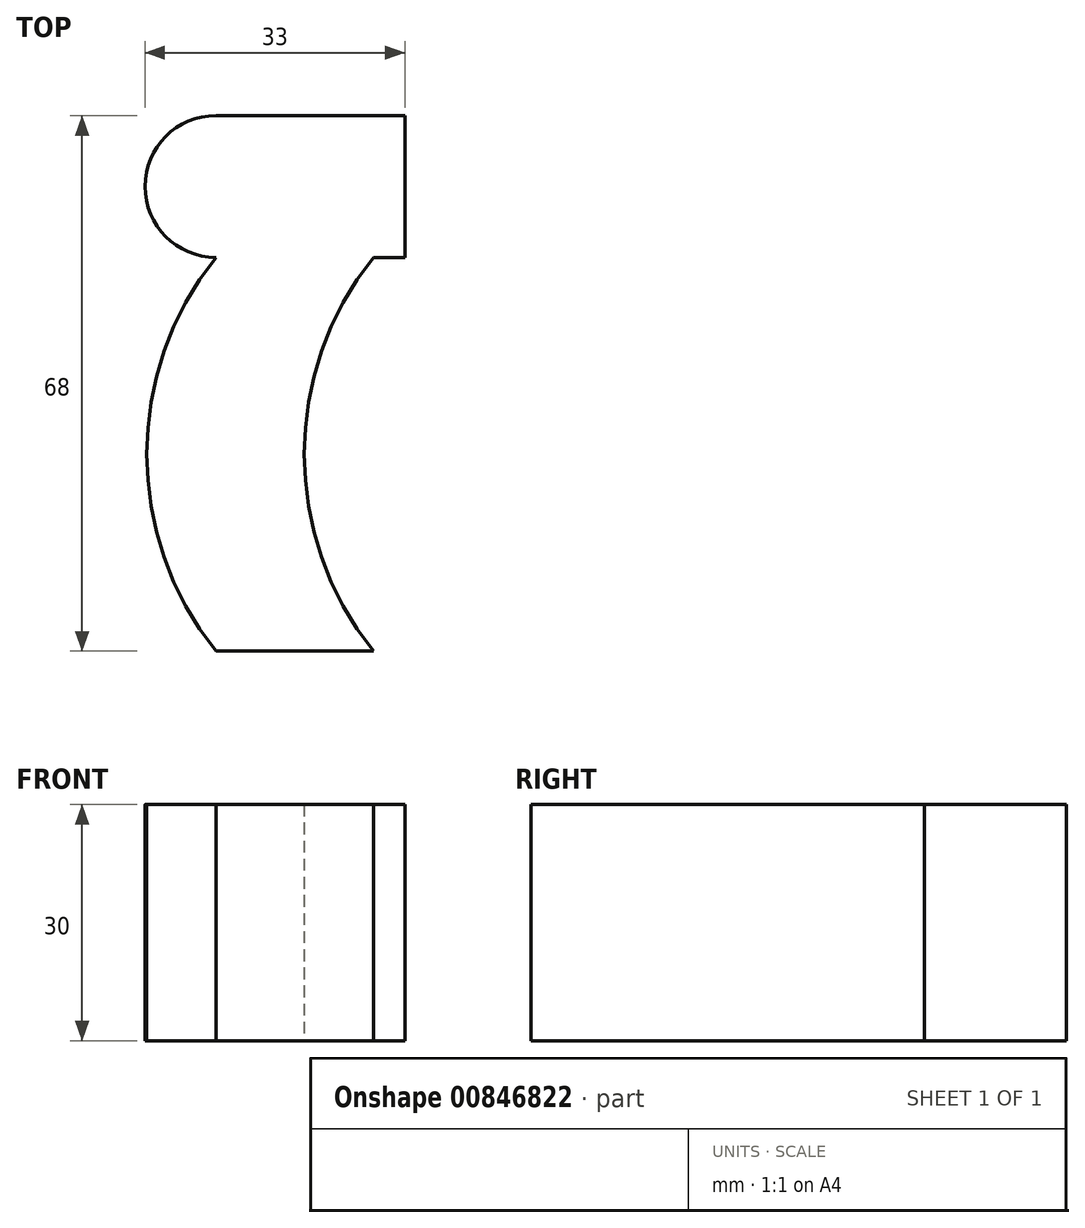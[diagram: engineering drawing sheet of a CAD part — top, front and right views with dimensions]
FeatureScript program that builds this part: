
annotation { "Feature Type Name" : "Feature", "Feature Type Description" : "" }
export const myFeature = defineFeature(function(context is Context, id is Id, definition is map)
    precondition{}
    {
        {
            var Q0;
            Q0=qCreatedBy(makeId("Top.planeOp"),FACE);
            var sketch = newSketch(context, id + "F0", { "sketchPlane" : qUnion([Q0])});
            skLineSegment(sketch, "E0", {"start": v(-2.92, -33.1) * mm, "end": v(17.08, -33.1) * mm});
            skArc(sketch, "E1", {"start": v(-2.92, 16.9) * mm, "mid": v(-11.7, -8.1) * mm, "end": v(-2.92, -33.1) * mm});
            skArc(sketch, "E2", {"start": v(17.08, 16.9) * mm, "mid": v(8.3, -8.1) * mm, "end": v(17.08, -33.1) * mm});
            skLineSegment(sketch, "E3", {"start": v(17.08, 16.9) * mm, "end": v(21.08, 16.9) * mm});
            skLineSegment(sketch, "E4", {"start": v(21.08, 16.9) * mm, "end": v(21.08, 34.9) * mm});
            skLineSegment(sketch, "E5", {"start": v(21.08, 34.9) * mm, "end": v(-2.92, 34.9) * mm});
            skArc(sketch, "E6", {"start": v(-2.92, 34.9) * mm, "mid": v(-11.92, 25.9) * mm, "end": v(-2.92, 16.9) * mm});
            skSolve(sketch);
        }
        {
            var Q0;
            Q0=makeQuery(id+"F0.imprint","IMPRINT",FACE,{"disambiguationData":[TD([[makeQuery(id+"F0.imprint","IMPRINT",EDGE,{"derivedFrom":sQuery(id+"F0.wireOp",EDGE,"E0")}),1.0]])]});
            extrude(context, id + "F1", {"entities" : qUnion([Q0]), "endBound" : BoundingType.SYMMETRIC, "depth" : 30 * mm, "offsetDistance" : 25 * mm});
        }
    });
